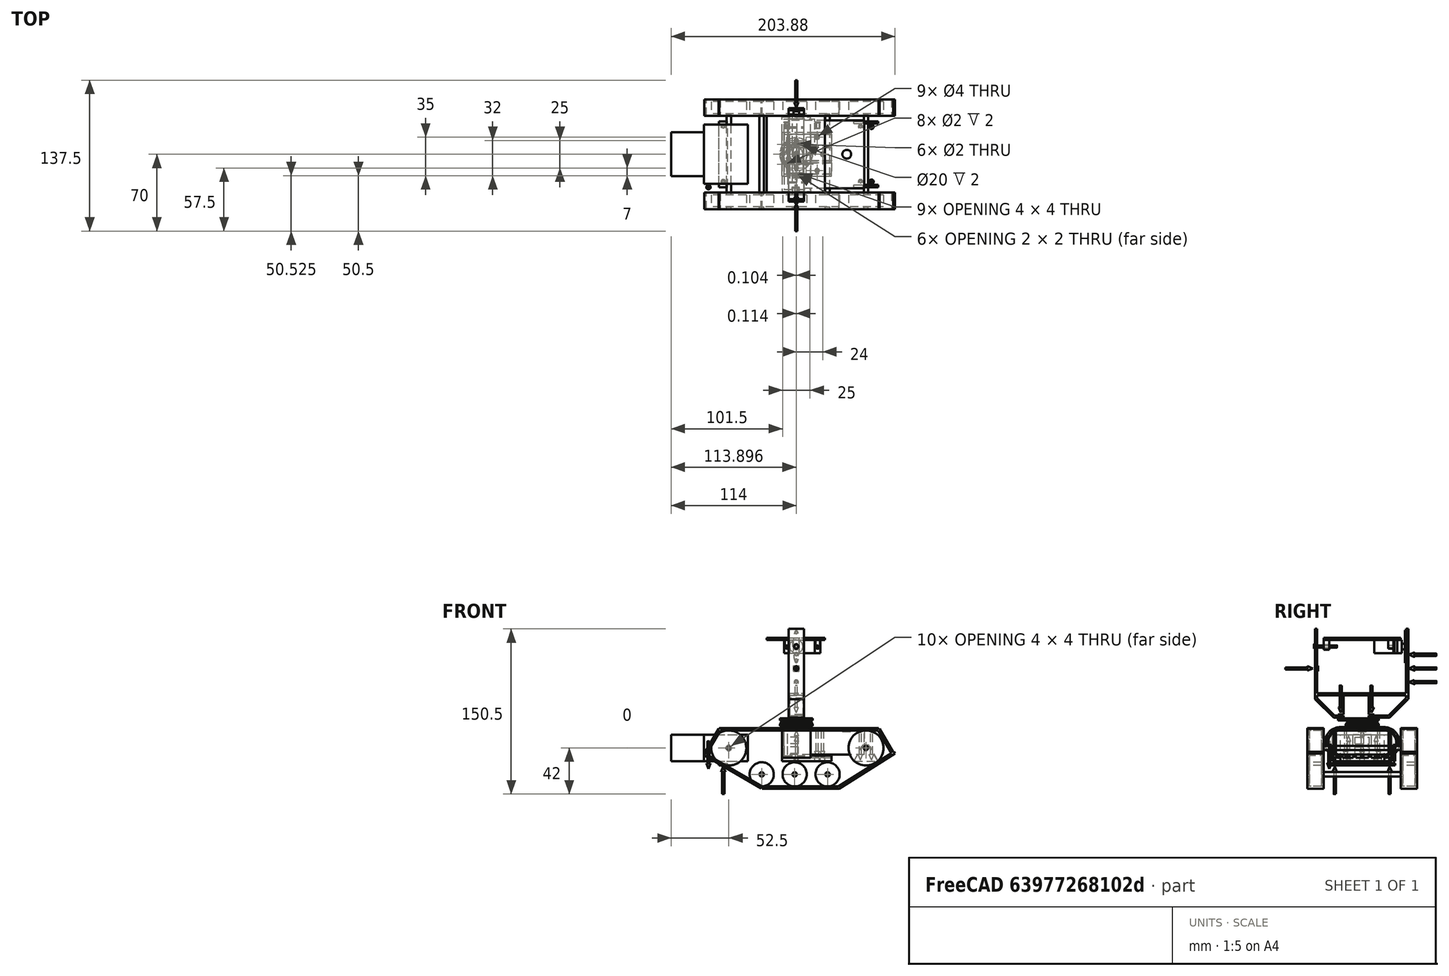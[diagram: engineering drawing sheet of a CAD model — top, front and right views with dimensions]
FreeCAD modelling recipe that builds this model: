
FCSTD DOCUMENT
Label: androidtank_11
License: CC-BY 3.0
LicenseURL: http://creativecommons.org/licenses/by/3.0/
objects: Part::Cylinder×59, Part::MultiFuse×47, Part::Box×40, Part::Cut×9, Part::Sphere×8, App::DocumentObjectGroup×3, Part::FeaturePython×1, Mesh::Feature×1, Part::Cone×1
note: 165 computed .brp shape members not serialized (recipe doc carries the construction recipe); baked Part::Feature solids carry a one-line shape summary decoded from their .brp

FEATURE [Part::Box] Box001001  label="Moter Unit2"
  Height = 24
  Length = 30
  Placement = pos=(-34,10,2) rot=(0,0,1;0rad)
  Width = 40
FEATURE [Part::Cylinder] Cylinder  label="Shaft"
  Angle = 360
  Height = 100
  Placement = pos=(20,-20,14) rot=(-1,0,0;1.5708rad)
  Radius = 2
FEATURE [Part::Box] Box001002
  Height = 2
  Length = 145
  Placement = pos=(10,-20,30) rot=(0,0,1;0rad)
  Width = 15
FEATURE [Part::Box] Box001002001
  Height = 2
  Length = 70
  Placement = pos=(49,-20,-23) rot=(0,0,1;0rad)
  Width = 15
FEATURE [Part::Box] Box001002001001
  Height = 2
  Length = 60
  Placement = pos=(119,-20,-23) rot=(0,-1,0;0.558505rad)
  Width = 15
FEATURE [Part::Box] Box001002001002
  Height = 2
  Length = 60
  Placement = pos=(49,-20,-21) rot=(0,1,0;3.66519rad)
  Width = 15
FEATURE [Part::Box] Box001002001003
  Height = 2
  Length = 26
  Placement = pos=(-2,-20,8) rot=(0,-1,0;1.0472rad)
  Width = 15
FEATURE [Part::Box] Box001002001003001
  Height = 2
  Length = 26
  Placement = pos=(169,-20,9) rot=(0,-1,0;2.0944rad)
  Width = 15
FEATURE [Part::MultiFuse] Fusion002001002  label="Caterpiller1"
  Shapes = -> [Box001002,Box001002001,Box001002001002,Box001002001001,Box001002001003,Box001002001003001]
FEATURE [Part::MultiFuse] Fusion002001002001  label="Caterpiller2"
  Placement = pos=(0,85,0) rot=(0,0,1;0rad)
  Shapes = -> [Box001002,Box001002001,Box001002001002,Box001002001001,Box001002001003,Box001002001003001]
FEATURE [Part::Cylinder] Cylinder002001001002  label="Wheel006"
  Angle = 360
  Height = 11
  Placement = pos=(20,78,14) rot=(1,0,0;1.5708rad)
  Radius = 11
FEATURE [Part::Cylinder] Cylinder002001001002001  label="Wheel007"
  Angle = 360
  Height = 11
  Placement = pos=(20,-7,14) rot=(1,0,0;1.5708rad)
  Radius = 11
FEATURE [Part::Cylinder] Cylinder002001002001  label="Shaft002"
  Angle = 360
  Height = 100
  Placement = pos=(20,-20,14) rot=(-1,0,0;1.5708rad)
  Radius = 2
FEATURE [Part::MultiFuse] Fusion002001002002002  label="SWheelSet1"
  Placement = pos=(28.5,0,-24) rot=(0,0,1;0rad)
  Shapes = -> [Cylinder002001002001,Cylinder002001001002,Cylinder002001001002001]
FEATURE [Part::MultiFuse] Fusion002001002002002001  label="SWheelSet2"
  Placement = pos=(58.5,0,-24) rot=(0,0,1;0rad)
  Shapes = -> [Cylinder002001002001,Cylinder002001001002,Cylinder002001001002001]
FEATURE [Part::MultiFuse] Fusion002001002002002001001  label="SWheelSet3"
  Placement = pos=(88.5,0,-24) rot=(0,0,1;0rad)
  Shapes = -> [Cylinder002001002001,Cylinder002001001002,Cylinder002001001002001]
FEATURE [Part::Box] Box001002001003002
  Height = 22
  Length = 70
  Placement = pos=(0,0,-11) rot=(0,0,1;0rad)
  Width = 40
FEATURE [Part::Cylinder] Cylinder002001001002002
  Angle = 360
  Height = 70
  Placement = pos=(0,0,0) rot=(0,1,0;1.5708rad)
  Radius = 11
FEATURE [Part::Cylinder] Cylinder001
  Angle = 360
  Height = 70
  Placement = pos=(0,40,0) rot=(0,1,0;1.5708rad)
  Radius = 11
FEATURE [Part::Cylinder] Cylinder002001001002003  label="PowerButton"
  Angle = 360
  Height = 2
  Placement = pos=(16,20,10) rot=(0,0,1;0rad)
  Radius = 4
FEATURE [Part::Box] Box001002001003003  label="USB1"
  Height = 6
  Length = 15
  Placement = pos=(60,13.5,-1) rot=(0,0,1;0rad)
  Width = 13
FEATURE [Part::Box] Box001001001  label="USB2"
  Height = 6
  Length = 15
  Placement = pos=(60,13.5,-10) rot=(0,0,1;0rad)
  Width = 13
FEATURE [Part::MultiFuse] Fusion002001002002002001002
  Shapes = -> [Cylinder001,Box001002001003002,Cylinder002001001002002]
FEATURE [Part::MultiFuse] Fusion001001
  Shapes = -> [Box001001001,Cylinder002001001002003,Box001002001003003]
FEATURE [Part::Cut] Cut  label="Eneloop"
  Base = -> Fusion002001002002002001002
  Placement = pos=(142,50,19) rot=(0,0,1;3.14159rad)
  Tool = -> Fusion001001
FEATURE [Part::Cylinder] Cylinder001001  label="Cylinder002"
  Angle = 360
  Height = 26
  Placement = pos=(0,50,19) rot=(0,1,0;1.5708rad)
  Radius = 14
FEATURE [Part::Box] Box001002001003002001  label="Box001002001003002001001001001006001001002001003001006001003"
  Height = 28
  Length = 26
  Placement = pos=(0,10,5) rot=(0,0,1;0rad)
  Width = 40
FEATURE [Part::Cylinder] Cylinder002001001002002001  label="Cylinder003"
  Angle = 360
  Height = 26
  Placement = pos=(0,10,19) rot=(0,1,0;1.5708rad)
  Radius = 14
FEATURE [Part::Box] Box001  label="Moter Unit1"
  Height = 24
  Length = 40
  Placement = pos=(-4,3,2) rot=(0,0,1;0rad)
  Width = 54
FEATURE [Part::Box] Box001002001003002001001  label="Box003"
  Height = 5
  Length = 45
  Placement = pos=(0,10,2) rot=(0,0,1;0rad)
  Width = 40
FEATURE [Part::Box] Box001002001003002001002  label="Box004"
  Height = 24
  Length = 26
  Placement = pos=(2,10,7) rot=(0,0,1;0rad)
  Width = 40
FEATURE [Part::Cylinder] Cylinder001001001  label="Cylinder004"
  Angle = 360
  Height = 26
  Placement = pos=(2,50,19) rot=(0,1,0;1.5708rad)
  Radius = 12
FEATURE [Part::Cylinder] Cylinder002001001002002001001  label="Cylinder005"
  Angle = 360
  Height = 26
  Placement = pos=(2,10,19) rot=(0,1,0;1.5708rad)
  Radius = 12
FEATURE [Part::Box] Box001002001003002001001001  label="Box006"
  Height = 3
  Length = 45
  Placement = pos=(2,12,5) rot=(0,0,1;0rad)
  Width = 10
FEATURE [Part::Box] Box001002001003002001001001001  label="Box007"
  Height = 3
  Length = 45
  Placement = pos=(2,24,5) rot=(0,0,1;0rad)
  Width = 12
FEATURE [Part::Box] Box001002001003002001001001001001  label="Box008"
  Height = 3
  Length = 45
  Placement = pos=(2,38,5) rot=(0,0,1;0rad)
  Width = 10
FEATURE [Part::MultiFuse] Fusion002001002002002001003
  Shapes = -> [Box001002001003002001,Cylinder001001,Cylinder002001001002002001,Box001002001003002001001]
FEATURE [Part::Cylinder] Cylinder002001001002002001002001  label="Cylinder007"
  Angle = 360
  Height = 40
  Placement = pos=(80,17.5,0) rot=(0,0,1;0rad)
  Radius = 1
FEATURE [Part::Cylinder] Cylinder002001001002002001002  label="Cylinder006"
  Angle = 360
  Height = 40
  Placement = pos=(80,42.5,0) rot=(0,0,1;0rad)
  Radius = 1
FEATURE [Part::Cylinder] Cylinder002001001002002001002001001  label="Cylinder008"
  Angle = 360
  Height = 40
  Placement = pos=(104,30,0) rot=(0,0,1;0rad)
  Radius = 2
FEATURE [Part::Cylinder] Cylinder002001001002002001002001002  label="Cylinder009"
  Angle = 360
  Height = 40
  Placement = pos=(99,45.5,0) rot=(0,0,1;0rad)
  Radius = 2
FEATURE [Part::Cylinder] Cylinder002001001002002001002001003  label="Cylinder0010"
  Angle = 360
  Height = 40
  Placement = pos=(99,15,0) rot=(0,0,1;0rad)
  Radius = 2
FEATURE [Part::Box] Box001002001003002001001001001006  label="Box009"
  Height = 2
  Length = 53
  Placement = pos=(47,-5,100) rot=(0,0,1;0rad)
  Width = 70
FEATURE [Part::Box] Box001002001003002001001001001006001  label="Box010"
  Height = 64
  Length = 14
  Placement = pos=(67,70,66) rot=(0,0,1;0rad)
  Width = 2
FEATURE [Part::Box] Box001002001003002001001001001006001001  label="Box011"
  Height = 2
  Length = 13
  Placement = pos=(67.5,12.5,48) rot=(0,0,1;0rad)
  Width = 23.5
FEATURE [Part::Box] Box001002001003002001001001001006001001001  label="Box012"
  Height = 64
  Length = 14
  Placement = pos=(67,-13,66) rot=(0,0,1;0rad)
  Width = 2
FEATURE [Part::Cylinder] Cylinder002001001002002001002001008  label="Hole1"
  Angle = 360
  Height = 20
  Placement = pos=(74,-20,114) rot=(-1,0,0;1.5708rad)
  Radius = 1.5
FEATURE [Part::Cylinder] Cylinder002001001002002001002001008001  label="Hole2"
  Angle = 360
  Height = 20
  Placement = pos=(74,60,126.5) rot=(-1,0,0;1.5708rad)
  Radius = 1
FEATURE [Part::Cylinder] Cylinder002001001002002001002001008001001  label="Hole4"
  Angle = 360
  Height = 20
  Placement = pos=(74,38.5,41) rot=(0,0,1;0rad)
  Radius = 1
FEATURE [Part::Cylinder] Cylinder002001001002002001002001008001001001  label="Hole3"
  Angle = 360
  Height = 20
  Placement = pos=(74,60,101.5) rot=(-1,0,0;1.5708rad)
  Radius = 1
FEATURE [Part::Cylinder] Cylinder002001001002002001002001008001001002  label="Hole5"
  Angle = 360
  Height = 20
  Placement = pos=(74,10.5,41) rot=(0,0,1;0rad)
  Radius = 1
FEATURE [Part::Box] Box001002001003002001001001001006001001001001  label="Box013"
  Height = 24
  Length = 14
  Placement = pos=(67,4,49) rot=(1,0,0;0.785397rad)
  Width = 2
FEATURE [Part::Box] Box001002001003002001001001001006001001001001001  label="Box014"
  Height = 24
  Length = 14
  Placement = pos=(67,53.41,50.41) rot=(-1,0,0;0.785397rad)
  Width = 2
FEATURE [Part::Box] Box001002001003002001001001001006001001002001  label="Box016"
  Height = 2
  Length = 14
  Placement = pos=(67,4,49) rot=(0,0,1;0rad)
  Width = 9
FEATURE [Part::Box] Box001002001003002001001001001006001001002001001  label="Box017"
  Height = 2
  Length = 14
  Placement = pos=(67,36,49) rot=(0,0,1;0rad)
  Width = 19
FEATURE [Part::Box] Box001002001003002001001001001006001001002001002  label="Box015"
  Height = 2
  Length = 14
  Placement = pos=(67,-13,69.5) rot=(0,0,1;0rad)
  Width = 85
FEATURE [Part::MultiFuse] Fusion002001002002002001009
  Shapes = -> [Box001002001003002001001001001006001,Box001002001003002001001001001006001001001001,Box001002001003002001001001001006001001001,Box001002001003002001001001001006001001001001001,Box001002001003002001001001001006001001002001,Box001002001003002001001001001006001001002001002,Box001002001003002001001001001006001001002001001]
FEATURE [Part::Cylinder] Cylinder002001001002002001002001008001001002001  label="Hole006"
  Angle = 360
  Height = 20
  Placement = pos=(74,10.5,60) rot=(0,0,1;0rad)
  Radius = 2
FEATURE [Part::Cylinder] Cylinder002001001002002001002001008001001002002  label="Hole007"
  Angle = 360
  Height = 20
  Placement = pos=(74,38.5,60) rot=(0,0,1;0rad)
  Radius = 2
FEATURE [Part::MultiFuse] Fusion002001002002002001010
  Shapes = -> [Cylinder002001001002002001002001008001,Box001002001003002001001001001006001001,Cylinder002001001002002001002001008001001,Cylinder002001001002002001002001008,Cylinder002001001002002001002001008001001001,Cylinder002001001002002001002001008001001002,Cylinder002001001002002001002001008001001002002,Cylinder002001001002002001002001008001001002001]
FEATURE [Part::Cut] Cut003  label="HeadFrame"
  Base = -> Fusion002001002002002001009
  Placement = pos=(6,0,-7.5) rot=(0,0,1;0rad)
  Tool = -> Fusion002001002002002001010
FEATURE [Part::Cylinder] Cylinder002001001002002001002001008001001002003  label="Cylinder025"
  Angle = 360
  Height = 5
  Placement = pos=(74,0,94) rot=(1,0,0;1.5708rad)
  Radius = 3
FEATURE [Part::Box] Box001002001003002001001001001006001001002001003  label="Box020"
  Height = 6
  Length = 6
  Placement = pos=(71,-5,94) rot=(0,0,1;0rad)
  Width = 5
FEATURE [Part::Cylinder] Cylinder002001001002002001002001008001001002003001  label="Cylinder026"
  Angle = 360
  Height = 7
  Placement = pos=(74,1,94) rot=(1,0,0;1.5708rad)
  Radius = 1.5
FEATURE [Part::Box] Box001002001003002001001001001006001001002001003001001  label="Box022"
  Height = 6
  Length = 4
  Placement = pos=(91.5,53.5,94) rot=(0,0,1;0rad)
  Width = 5
FEATURE [Part::Cylinder] Cylinder002001001002002001002001008001001002003002  label="Cylinder027"
  Angle = 360
  Height = 5
  Placement = pos=(65.5,58.5,94) rot=(1,0,0;1.5708rad)
  Radius = 2
FEATURE [Part::Cylinder] Cylinder002001001002002001002001008001001002003002001  label="Cylinder028"
  Angle = 360
  Height = 5
  Placement = pos=(93.5,58.5,94) rot=(1,0,0;1.5708rad)
  Radius = 2
FEATURE [Part::Box] Box001002001003002001001001001006001001002001003001  label="Box021"
  Height = 6
  Length = 4
  Placement = pos=(63.5,53.5,94) rot=(0,0,1;0rad)
  Width = 5
FEATURE [Part::Cylinder] Cylinder002001001002002001002001008001001002003002002  label="Cylinder029"
  Angle = 360
  Height = 6
  Placement = pos=(65.5,59,94) rot=(1,0,0;1.5708rad)
  Radius = 1
FEATURE [Part::Cylinder] Cylinder002001001002002001002001008001001002003002001001  label="Cylinder030"
  Angle = 360
  Height = 6
  Placement = pos=(93.5,59,94) rot=(1,0,0;1.5708rad)
  Radius = 1
FEATURE [Part::MultiFuse] Fusion002001002002002001011
  Shapes = -> [Box001002001003002001001001001006,Box001002001003002001001001001006001001002001003001001,Cylinder002001001002002001002001008001001002003002001,Box001002001003002001001001001006001001002001003,Cylinder002001001002002001002001008001001002003,Box001002001003002001001001001006001001002001003001,Cylinder002001001002002001002001008001001002003002]
FEATURE [Part::MultiFuse] Fusion002001002002002001012
  Shapes = -> [Cylinder002001001002002001002001008001001002003001,Cylinder002001001002002001002001008001001002003002002,Cylinder002001001002002001002001008001001002003002001001]
FEATURE [Part::Cut] Cut002003  label="HeadMount"
  Base = -> Fusion002001002002002001011
  Placement = pos=(6,0,12.5) rot=(0,0,1;0rad)
  Tool = -> Fusion002001002002002001012
FEATURE [Part::Cylinder] Cylinder002001001002002001002001001001  label="Cylinder040"
  Angle = 360
  Height = 40
  Placement = pos=(80,30,0) rot=(0,0,1;0rad)
  Radius = 2
FEATURE [Part::Box] Box001002001003002001001001001006001001002001003001002  label="ServoBody"
  Height = 21
  Length = 23
  Width = 12
FEATURE [Part::Cylinder] Cylinder002001001002002001002001008001001002003002001002  label="ServoBody2"
  Angle = 360
  Height = 4
  Placement = pos=(6,6,21) rot=(0,0,1;0rad)
  Radius = 6
FEATURE [Part::Box] Box001002001003002001001001001006001001002001003001003  label="ServoBody3"
  Height = 1
  Length = 33
  Placement = pos=(-5,0,17.5) rot=(0,0,1;0rad)
  Width = 12
FEATURE [Part::Cylinder] Cylinder001001002  label="ServoAxis"
  Angle = 360
  Height = 4
  Placement = pos=(6,6,24) rot=(0,0,1;0rad)
  Radius = 2.5
FEATURE [Part::MultiFuse] Fusion005  label="ServoArmL"
  Shapes = -> [Cylinder001001002,Box001002001003002001001001001006001001002001003001003,Box001002001003002001001001001006001001002001003001002,Cylinder002001001002002001002001008001001002003002001002]
FEATURE [Part::MultiFuse] Fusion006  label="ServoYaw"
  Placement = pos=(86,36,62) rot=(0.707107,-0.707107,0;3.14159rad)
  Shapes = -> [Fusion005]
FEATURE [Part::Cylinder] Cylinder003001001004  label="Cylinder002001001002002001002001008001001002003002001006"
  Angle = 360
  Height = 0.5
  Placement = pos=(-2.5,6,20.5) rot=(0,0,1;0rad)
  Radius = 2
FEATURE [Part::Cylinder] Cylinder003001001005  label="Cylinder011"
  Angle = 360
  Height = 2
  Placement = pos=(6,6,21) rot=(0,0,1;0rad)
  Radius = 15
FEATURE [Part::Cylinder] Cylinder003001001004001  label="Cylinder010"
  Angle = 360
  Height = 0.5
  Placement = pos=(25.5,6,20.5) rot=(0,0,1;0rad)
  Radius = 2
FEATURE [Part::Cylinder] Cylinder003001001005001  label="Cylinder012"
  Angle = 360
  Height = 2
  Placement = pos=(6,6,21) rot=(0,0,1;0rad)
  Radius = 6.5
FEATURE [Part::Cylinder] Cylinder003001001005001001  label="Cylinder013"
  Angle = 360
  Height = 2
  Placement = pos=(12,6,21) rot=(0,0,1;0rad)
  Radius = 3.5
FEATURE [Part::Box] Box002
  Height = 2
  Length = 10
  Placement = pos=(18,3,21) rot=(0,0,1;0rad)
  Width = 6
FEATURE [Part::Cylinder] Cylinder003001001004002  label="Cylinder014"
  Angle = 360
  Height = 5
  Placement = pos=(-2.5,6,19.5) rot=(0,0,1;0rad)
  Radius = 1
FEATURE [Part::Cylinder] Cylinder003001001004001001  label="Cylinder015"
  Angle = 360
  Height = 5
  Placement = pos=(25.5,6,19.5) rot=(0,0,1;0rad)
  Radius = 1
FEATURE [Part::MultiFuse] Fusion008
  Shapes = -> [Cylinder003001001005,Box002,Cylinder003001001004,Cylinder003001001004001]
FEATURE [Part::MultiFuse] Fusion009
  Shapes = -> [Cylinder003001001005001,Cylinder003001001005001001,Cylinder003001001004002,Cylinder003001001004001001]
FEATURE [Part::Cut] Cut002  label="Guide1"
  Base = -> Fusion008
  Placement = pos=(86,36,62) rot=(-0.705662,0.708549,0;3.14159rad)
  Tool = -> Fusion009
FEATURE [Part::Box] Box001002001003002001001001001006001001002001003001004  label="ServoBody004"
  Height = 21
  Length = 23
  Width = 12
FEATURE [Part::Cylinder] Cylinder002001001002002001002001008001001002003002001003  label="ServoBody005"
  Angle = 360
  Height = 4
  Placement = pos=(6,6,21) rot=(0,0,1;0rad)
  Radius = 6
FEATURE [Part::Box] Box001002001003002001001001001006001001002001003001005  label="ServoBody006"
  Height = 1
  Length = 33
  Placement = pos=(-5,0,17.5) rot=(0,0,1;0rad)
  Width = 12
FEATURE [Part::Cylinder] Cylinder001001003  label="ServoAxis001"
  Angle = 360
  Height = 4
  Placement = pos=(6,6,24) rot=(0,0,1;0rad)
  Radius = 2.5
FEATURE [Part::MultiFuse] Fusion005001  label="ServoArmL001"
  Shapes = -> [Cylinder001001003,Box001002001003002001001001001006001001002001003001005,Box001002001003002001001001001006001001002001003001004,Cylinder002001001002002001002001008001001002003002001003]
FEATURE [Part::Cylinder] Cylinder002001001002002001002001008001001002003002001004  label="Cylinder002001001002002001002001008001001002003002001012"
  Angle = 360
  Height = 2
  Radius = 2.5
FEATURE [Part::FeaturePython] Scale  # Draft clone (typed FeaturePython)
  Objects = -> [Cylinder002001001002002001002001008001001002003002001004]
  Placement = pos=(0,0,1) rot=(0,0,1;0rad)
  Scale = (6,1,0.5)
FEATURE [Part::MultiFuse] Fusion  label="Arm"
  Placement = pos=(6,6,27) rot=(0,0,1;1.5708rad)
  Shapes = -> [Cylinder002001001002002001002001008001001002003002001004,Scale]
FEATURE [Part::MultiFuse] Fusion006001  label="ServoPitch"
  Placement = pos=(74,41,112.5) rot=(-1,0,0;1.5708rad)
  Shapes = -> [Fusion005001,Fusion]
FEATURE [Part::Cylinder] Cylinder002001001002002001002001008001001002003002001005  label="Wheel1"
  Angle = 360
  Height = 11
  Placement = pos=(20,78,14) rot=(1,0,0;1.5708rad)
  Radius = 16
FEATURE [Part::Cylinder] Cylinder002001001002002001002001008001001002003002001005001  label="Wheel2"
  Angle = 360
  Height = 11
  Placement = pos=(20,-7,14) rot=(1,0,0;1.5708rad)
  Radius = 16
FEATURE [Part::MultiFuse] Fusion002001002002002001014  label="LWheelSet1"
  Placement = pos=(-1.5,0,0) rot=(0,0,1;0rad)
  Shapes = -> [Cylinder,Cylinder002001001002002001002001008001001002003002001005,Cylinder002001001002002001002001008001001002003002001005001]
FEATURE [Part::MultiFuse] Fusion002001002002002001014001  label="LWheelSet2"
  Placement = pos=(123.5,0,0) rot=(0,0,1;0rad)
  Shapes = -> [Cylinder,Cylinder002001001002002001002001008001001002003002001005,Cylinder002001001002002001002001008001001002003002001005001]
FEATURE [Part::Cylinder] Cylinder003001001003  label="Cylinder002001001002002001002001008001001002003002001013"
  Angle = 360
  Height = 2
  Placement = pos=(6,6,26) rot=(0,0,1;0rad)
  Radius = 15
FEATURE [Part::Sphere] Sphere
  Angle1 = -90
  Angle2 = 0
  Angle3 = 360
  Placement = pos=(-3,-3,26) rot=(0,0,1;0rad)
  Radius = 2
FEATURE [Part::Sphere] Sphere001
  Angle1 = -90
  Angle2 = 0
  Angle3 = 360
  Placement = pos=(15,-3,26) rot=(0,0,1;0rad)
  Radius = 2
FEATURE [Part::Sphere] Sphere001001  label="Sphere002"
  Angle1 = -90
  Angle2 = 0
  Angle3 = 360
  Placement = pos=(15,15,26) rot=(0,0,1;0rad)
  Radius = 2
FEATURE [Part::Sphere] Sphere001001001  label="Sphere003"
  Angle1 = -90
  Angle2 = 0
  Angle3 = 360
  Placement = pos=(-3,15,26) rot=(0,0,1;0rad)
  Radius = 2
FEATURE [Part::Cylinder] Cylinder003001001005001004  label="Cylinder020"
  Angle = 360
  Height = 4
  Placement = pos=(-6.5,6,26) rot=(0,0,1;0rad)
  Radius = 1
FEATURE [Part::Cylinder] Cylinder003001001001003  label="Cylinder021"
  Angle = 360
  Height = 4
  Placement = pos=(18.5,6,26) rot=(0,0,1;0rad)
  Radius = 1
FEATURE [Part::Cylinder] Cylinder003001001005001003001  label="Cylinder022"
  Angle = 360
  Height = 5
  Placement = pos=(-3,-3,26) rot=(0,0,1;0rad)
  Radius = 1
FEATURE [Part::Cylinder] Cylinder003001001001002001  label="Cylinder023"
  Angle = 360
  Height = 5
  Placement = pos=(15,-3,26) rot=(0,0,1;0rad)
  Radius = 1
FEATURE [Part::Sphere] Sphere001001001001  label="Sphere004"
  Angle1 = -90
  Angle2 = 0
  Angle3 = 360
  Placement = pos=(-6.5,6,26) rot=(0,0,1;0rad)
  Radius = 2
FEATURE [Part::Sphere] Sphere001001001001001  label="Sphere005"
  Angle1 = -90
  Angle2 = 0
  Angle3 = 360
  Placement = pos=(18.5,6,26) rot=(0,0,1;0rad)
  Radius = 2
FEATURE [Part::Sphere] Sphere001001001001001001  label="Sphere006"
  Angle1 = -90
  Angle2 = 0
  Angle3 = 360
  Placement = pos=(6,-6.5,26) rot=(0,0,1;0rad)
  Radius = 2
FEATURE [Part::Sphere] Sphere001001001001001001001  label="Sphere007"
  Angle1 = -90
  Angle2 = 0
  Angle3 = 360
  Placement = pos=(6,18.5,26) rot=(0,0,1;0rad)
  Radius = 2
FEATURE [Part::Cylinder] Cylinder003001001003001  label="Cylinder024"
  Angle = 360
  Height = 2
  Placement = pos=(6,6,26) rot=(0,0,1;0rad)
  Radius = 10
FEATURE [Part::MultiFuse] Fusion014
  Shapes = -> [Sphere,Cylinder003001001003,Sphere001001001,Sphere001001001001001001,Sphere001001001001,Sphere001,Sphere001001,Sphere001001001001001001001,Sphere001001001001001]
FEATURE [Part::Cylinder] Cylinder003001001005001003001001  label="Cylinder002001001002002001002001008001001002003002001014"
  Angle = 360
  Height = 5
  Placement = pos=(-3,15,26) rot=(0,0,1;0rad)
  Radius = 1
FEATURE [Part::Cylinder] Cylinder003001001001002001001  label="Cylinder002001001002002001002001008001001002003002001015"
  Angle = 360
  Height = 5
  Placement = pos=(15,15,26) rot=(0,0,1;0rad)
  Radius = 1
FEATURE [Part::Cylinder] Cylinder003001001005001003001001001  label="Cylinder002001001002002001002001008001001002003002001016"
  Angle = 360
  Height = 5
  Placement = pos=(6,18.5,26) rot=(0,0,1;0rad)
  Radius = 1
FEATURE [Part::Cylinder] Cylinder003001001005001003001001001001  label="Cylinder002001001002002001002001008001001002003002001017"
  Angle = 360
  Height = 5
  Placement = pos=(6,-6.5,26) rot=(0,0,1;0rad)
  Radius = 1
FEATURE [Part::MultiFuse] Fusion015
  Shapes = -> [Cylinder003001001003001,Cylinder003001001005001004,Cylinder003001001001003,Cylinder003001001005001003001,Cylinder003001001001002001,Cylinder003001001005001003001001,Cylinder003001001005001003001001001001,Cylinder003001001001002001001,Cylinder003001001005001003001001001]
FEATURE [Part::Cut] Cut002005  label="Guide2"
  Base = -> Fusion014
  Placement = pos=(74,36,62) rot=(1,0,0;3.14159rad)
  Tool = -> Fusion015
FEATURE [Part::MultiFuse] Fusion002001002002002001014002
  Shapes = -> [Box001002001003002001002,Cylinder001001001,Cylinder002001001002002001001,Box001002001003002001001001,Box001002001003002001001001001,Box001002001003002001001001001001]
FEATURE [Part::Cut] Cut002006
  Base = -> Fusion002001002002002001003
  Placement = pos=(67,0,0) rot=(0,0,1;0rad)
  Tool = -> Fusion002001002002002001014002
FEATURE [Part::Cylinder] Cylinder002001001002002001002001001001001  label="Cylinder041"
  Angle = 360
  Height = 20
  Placement = pos=(80,42.5,0) rot=(0,0,1;0rad)
  Radius = 2
FEATURE [Part::Cylinder] Cylinder002001001002002001002001001001001001  label="Cylinder042"
  Angle = 360
  Height = 20
  Placement = pos=(80,17.5,0) rot=(0,0,1;0rad)
  Radius = 2
FEATURE [Part::Box] Box001002001003003001  label="USB003"
  Height = 10
  Length = 15
  Placement = pos=(60,21.5,16) rot=(0,0,1;0rad)
  Width = 17
FEATURE [Part::MultiFuse] Fusion002001002002002001014003
  Shapes = -> [Cylinder002001001002002001002001,Cylinder002001001002002001002,Cylinder002001001002002001002001001,Cylinder002001001002002001002001002,Cylinder002001001002002001002001003,Cylinder002001001002002001002001001001,Cylinder002001001002002001002001001001001,Box001002001003003001,Cylinder002001001002002001002001001001001001]
FEATURE [Part::Cut] Cut002007  label="BatteryFrame2"
  Base = -> Cut002006
  Tool = -> Fusion002001002002002001014003
FEATURE [Part::Box] Box001002001003002001001001001006001001002001003001006  label="Box040"
  Height = 15
  Length = 22
  Placement = pos=(0,0,2) rot=(0,0,1;0rad)
  Width = 2
FEATURE [Part::Box] Box001002001003002001001001001006001001002001003001006001  label="Box041"
  Height = 20
  Length = 10
  Placement = pos=(22,0,2) rot=(0,-1,0;0.523599rad)
  Width = 2
FEATURE [Part::Box] Box001002001003002001001001001006001001002001003001006001001  label="Box042"
  Height = 20
  Length = 10
  Placement = pos=(-8.71,0,7) rot=(0,1,0;0.523599rad)
  Width = 2
FEATURE [Part::MultiFuse] Fusion002001002002002001014004
  Shapes = -> [Box001002001003002001001001001006001001002001003001006001001,Box001002001003002001001001001006001001002001003001006001]
FEATURE [Part::Cut] Cut002008  label="LWheelMount1"
  Base = -> Box001002001003002001001001001006001001002001003001006
  Placement = pos=(132.5,0,0) rot=(0,0,1;0rad)
  Tool = -> Fusion002001002002002001014004
FEATURE [Part::Cut] Cut002008001  label="LWheelMount2"
  Base = -> Box001002001003002001001001001006001001002001003001006
  Placement = pos=(132.5,58,0) rot=(0,0,1;0rad)
  Tool = -> Fusion002001002002002001014004
FEATURE [Mesh::Feature] UniversalPlate
FEATURE [Part::Box] Box  label="MotorMount"
  Height = 2
  Length = 8
  Placement = pos=(9.5,0,-2) rot=(0,0,1;0rad)
  Width = 60
FEATURE [App::DocumentObjectGroup] ____________  label="DriveFrame"
  Group = -> [Box001,Box001001,Fusion002001002,Fusion002001002001,Fusion002001002002002,Fusion002001002002002001,Fusion002001002002002001001,Fusion002001002002002001014,Fusion002001002002002001014001,Cut002008,Cut002008001,UniversalPlate,Box]
FEATURE [Part::Cone] Cone
  Angle = 360
  Height = 5
  Placement = pos=(0,0,-5) rot=(0,0,1;0rad)
  Radius1 = 0
  Radius2 = 2
FEATURE [Part::Cylinder] Cylinder002001001002002001002001008001001002003002001005002
  Angle = 360
  Height = 20
  Radius = 1
FEATURE [Part::MultiFuse] Fusion002001002002002001014005  label="ArrowOrig"
  Shapes = -> [Cone,Cylinder002001001002002001002001008001001002003002001005002]
FEATURE [Part::MultiFuse] Fusion002001002002002001014005001  label="Arrow001"
  Placement = pos=(148.5,5,8) rot=(0,0,1;0rad)
  Shapes = -> [Cone,Cylinder002001001002002001002001008001001002003002001005002]
FEATURE [Part::MultiFuse] Fusion002001002002002001014005001001  label="Arrow002"
  Placement = pos=(138.5,5,8) rot=(0,0,1;0rad)
  Shapes = -> [Cone,Cylinder002001001002002001002001008001001002003002001005002]
FEATURE [Part::MultiFuse] Fusion002001002002002001014005001002  label="Arrow003"
  Placement = pos=(148.5,55,8) rot=(0,0,1;0rad)
  Shapes = -> [Cone,Cylinder002001001002002001002001008001001002003002001005002]
FEATURE [Part::MultiFuse] Fusion002001002002002001014005001002001  label="Arrow004"
  Placement = pos=(138.5,55,8) rot=(0,0,1;0rad)
  Shapes = -> [Cone,Cylinder002001001002002001002001008001001002003002001005002]
FEATURE [Part::MultiFuse] Fusion002001002002002001014005001002002  label="Arrow005"
  Placement = pos=(13.5,5,-8) rot=(1,0,0;3.14159rad)
  Shapes = -> [Cone,Cylinder002001001002002001002001008001001002003002001005002]
FEATURE [Part::MultiFuse] Fusion002001002002002001014005001002002001  label="Arrow006"
  Placement = pos=(13.5,55,-8) rot=(1,0,0;3.14159rad)
  Shapes = -> [Cone,Cylinder002001001002002001002001008001001002003002001005002]
FEATURE [Part::MultiFuse] Fusion002001002002002001014005001002002002  label="Arrow007"
  Placement = pos=(80,17.5,20) rot=(1,0,0;3.14159rad)
  Shapes = -> [Cone,Cylinder002001001002002001002001008001001002003002001005002]
FEATURE [Part::MultiFuse] Fusion002001002002002001014005001002002002001  label="Arrow008"
  Placement = pos=(80,42.5,20) rot=(1,0,0;3.14159rad)
  Shapes = -> [Cone,Cylinder002001001002002001002001008001001002003002001005002]
FEATURE [Part::MultiFuse] Fusion002001002002002001014005001002002002002  label="Arrow009"
  Placement = pos=(80,10.5,51) rot=(0,0,1;0rad)
  Shapes = -> [Cone,Cylinder002001001002002001002001008001001002003002001005002]
FEATURE [Part::MultiFuse] Fusion002001002002002001014005001002002002003  label="Arrow010"
  Placement = pos=(80,38.5,51) rot=(0,0,1;0rad)
  Shapes = -> [Cone,Cylinder002001001002002001002001008001001002003002001005002]
FEATURE [Part::MultiFuse] Fusion002001002002002001014005001002002002002001  label="Arrow011"
  Placement = pos=(80,77.5,86.5) rot=(-1,0,0;1.5708rad)
  Shapes = -> [Cone,Cylinder002001001002002001002001008001001002003002001005002]
FEATURE [Part::MultiFuse] Fusion002001002002002001014005001002002002002001001  label="Arrow012"
  Placement = pos=(80,77.5,99) rot=(-1,0,0;1.5708rad)
  Shapes = -> [Cone,Cylinder002001001002002001002001008001001002003002001005002]
FEATURE [Part::MultiFuse] Fusion002001002002002001014005001002002002002001001001  label="Arrow013"
  Placement = pos=(80,77.5,74) rot=(-1,0,0;1.5708rad)
  Shapes = -> [Cone,Cylinder002001001002002001002001008001001002003002001005002]
FEATURE [Part::MultiFuse] Fusion002001002002002001014005001002002002002001001002  label="Arrow014"
  Placement = pos=(80,-20,86.5) rot=(1,0,0;1.5708rad)
  Shapes = -> [Cone,Cylinder002001001002002001002001008001001002003002001005002]
FEATURE [Part::MultiFuse] Fusion002001002002002001014005001002002002002001001003  label="Arrow015"
  Placement = pos=(80,30,25) rot=(1,0,0;3.14159rad)
  Shapes = -> [Cone,Cylinder002001001002002001002001008001001002003002001005002]
FEATURE [Part::MultiFuse] Fusion002001002002002001014005001002002002002001001004  label="Arrow016"
  Placement = pos=(104,30,11) rot=(0,0,1;0rad)
  Shapes = -> [Cone,Cylinder002001001002002001002001008001001002003002001005002]
FEATURE [Part::MultiFuse] Fusion002001002002002001014005001002002002002001001004001  label="Arrow017"
  Placement = pos=(99,45,11) rot=(0,0,1;0rad)
  Shapes = -> [Cone,Cylinder002001001002002001002001008001001002003002001005002]
FEATURE [Part::MultiFuse] Fusion002001002002002001014005001002002002002001001004001001  label="Arrow018"
  Placement = pos=(99,15,11) rot=(0,0,1;0rad)
  Shapes = -> [Cone,Cylinder002001001002002001002001008001001002003002001005002]
FEATURE [App::DocumentObjectGroup] ____________001  label="Arrows"
  Group = -> [Fusion002001002002002001014005,Fusion002001002002002001014005001,Fusion002001002002002001014005001001,Fusion002001002002002001014005001002,Fusion002001002002002001014005001002001,Fusion002001002002002001014005001002002,Fusion002001002002002001014005001002002001,Fusion002001002002002001014005001002002002,Fusion002001002002002001014005001002002002001,Fusion002001002002002001014005001002002002002,+9 more]
FEATURE [Part::MultiFuse] Fusion002001002002002001014005001002002002002001001004001002  label="Arm001"
  Placement = pos=(80,30,35) rot=(0.707107,0.707107,0;3.14159rad)
  Shapes = -> [Cylinder002001001002002001002001008001001002003002001004,Scale]
FEATURE [Part::Cylinder] Cylinder002001001002002001002001008001001002003002001005003
  Angle = 360
  Height = 1
  Placement = pos=(0,0,-1) rot=(0,0,1;0rad)
  Radius = 2
FEATURE [Part::Cylinder] Cylinder002001001002002001002001008001001002003002001005003001
  Angle = 360
  Height = 20
  Radius = 1
FEATURE [Part::MultiFuse] Fusion002001002002002001014005001002002002002001001004001003  label="Vise"
  Placement = pos=(80,-13,106.5) rot=(-1,0,0;1.5708rad)
  Shapes = -> [Cylinder002001001002002001002001008001001002003002001005003,Cylinder002001001002002001002001008001001002003002001005003001]
FEATURE [Part::Box] Box001002001003002001001001001006001001002001003001006001002  label="Nat"
  Height = 5
  Length = 5
  Placement = pos=(77.5,-11,84) rot=(0,0,1;0rad)
  Width = 1
FEATURE [App::DocumentObjectGroup] ____________002  label="Guide"
  Group = -> [Fusion002001002002002001014005001002002002002001001004001002,Fusion002001002002002001014005001002002002002001001004001003,Box001002001003002001001001001006001001002001003001006001002]
